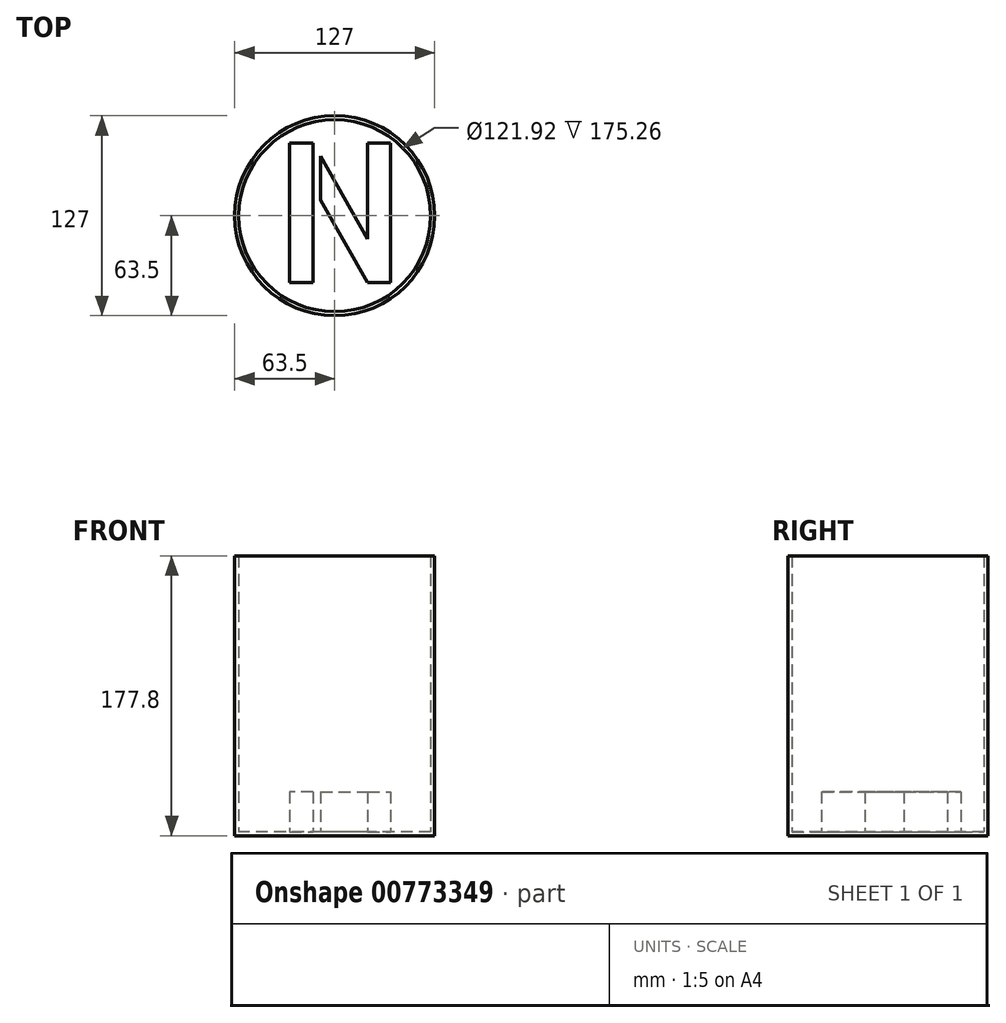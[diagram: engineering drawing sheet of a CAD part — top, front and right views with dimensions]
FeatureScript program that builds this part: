
annotation { "Feature Type Name" : "Feature", "Feature Type Description" : "" }
export const myFeature = defineFeature(function(context is Context, id is Id, definition is map)
    precondition{}
    {
        {
            var Q0;
            Q0=qCreatedBy(makeId("Top.planeOp"),FACE);
            var sketch = newSketch(context, id + "F0", { "sketchPlane" : qUnion([Q0])});
            skCircle(sketch, "E0", {"center": v(0, 0) * mm, "radius": 63.5 * mm});
            skSolve(sketch);
        }
        {
            var Q0;
            Q0=makeQuery(id+"F0.imprint","IMPRINT",FACE,{"disambiguationData":[TD([[makeQuery(id+"F0.imprint","IMPRINT",EDGE,{"derivedFrom":sQuery(id+"F0.wireOp",EDGE,"E0")}),1.0]])]});
            extrude(context, id + "F1", {"entities" : qUnion([Q0]), "depth" : 177.8 * mm, "offsetDistance" : 25.4 * mm});
        }
        {
            var Q0;
            Q0=makeQuery(id+"F1.opExtrude","CAP_FACE",FACE,{"disambiguationData":[OSD([sQuery(id+"F0.wireOp",EDGE,"E0")])],"isStart":false});
            shell(context, id + "F2", {"entities" : qUnion([Q0]), "thickness" : 2.54 * mm});
        }
        {
            var Q0;
            {var subQ0=sQuery(id+"F0.wireOp",EDGE,"E0");Q0=makeQuery(id+"F2.opShell","OFFSET_FACE",FACE,{"disambiguationData":[OSD([subQ0]),TDD([makeQuery(id+"F1.opExtrude","CAP_FACE",FACE,{"disambiguationData":[OSD([subQ0])],"isStart":true})])]});}
            var sketch = newSketch(context, id + "F3", { "sketchPlane" : qUnion([Q0])});
            skText(sketch, "E1", { "text": "N", "fontName": "AllertaStencil-Regular.ttf"});
            const initialGuessF3  = {"E1": [-0.0396, -0.04237, 1, 0, 0.0887]};
            skSetInitialGuess(sketch, initialGuessF3);
            skSolve(sketch);
        }
        {
            var Q0;
            Q0=makeQuery(id+"F3.imprint","IMPRINT",FACE,{"disambiguationData":[TD([[makeQuery(id+"F3.imprint","IMPRINT",EDGE,{"derivedFrom":sQuery(id+"F3.wireOp",EDGE,"E1.sketch_text.stroke-0")}),-1.0]])]});
            var Q1;
            Q1 = qSketchRegion(id + "F3", true);
            extrude(context, id + "F4", {"entities" : qUnion([Q0, Q1]), "operationType" : NewBodyOperationType.ADD, "depth" : 25.4 * mm, "offsetDistance" : 25.4 * mm});
        }
    });
